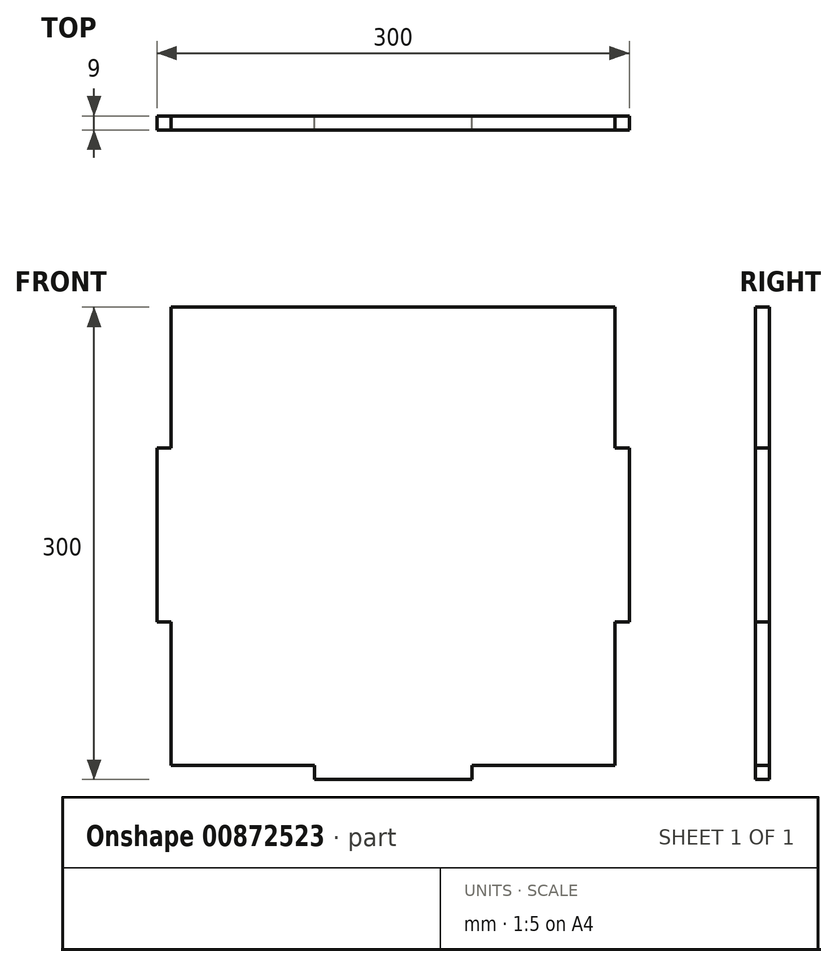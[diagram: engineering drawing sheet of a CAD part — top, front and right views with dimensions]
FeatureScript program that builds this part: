
annotation { "Feature Type Name" : "Feature", "Feature Type Description" : "" }
export const myFeature = defineFeature(function(context is Context, id is Id, definition is map)
    precondition{}
    {
        {
            var Q0;
            Q0=qCreatedBy(makeId("Front.planeOp"),FACE);
            var sketch = newSketch(context, id + "F0", { "sketchPlane" : qUnion([Q0])});
            skLineSegment(sketch, "E0.bottom", {"start": v(150, -150) * mm, "end": v(50, -150) * mm});
            skLineSegment(sketch, "E0.top", {"start": v(150, 150) * mm, "end": v(50, 150) * mm});
            skLineSegment(sketch, "E0.left", {"start": v(150, -150) * mm, "end": v(150, -50) * mm});
            skLineSegment(sketch, "E0.right", {"start": v(-150, -150) * mm, "end": v(-150, -50) * mm});
            skPoint(sketch, "E0.middle", {"position": v(0, 0) * mm});
            skLineSegment(sketch, "E1", {"start": v(-150, -50) * mm, "end": v(-141, -50) * mm});
            skLineSegment(sketch, "E2", {"start": v(-141, -50) * mm, "end": v(-141, 50) * mm});
            skLineSegment(sketch, "E3", {"start": v(-141, 50) * mm, "end": v(-150, 50) * mm});
            skLineSegment(sketch, "E4.trimOffspring", {"start": v(-150, 50) * mm, "end": v(-150, 150) * mm});
            skLineSegment(sketch, "E5", {"start": v(-50, 150) * mm, "end": v(-50, 141) * mm});
            skLineSegment(sketch, "E6", {"start": v(-50, 141) * mm, "end": v(50, 141) * mm});
            skLineSegment(sketch, "E7", {"start": v(50, 141) * mm, "end": v(50, 150) * mm});
            skLineSegment(sketch, "E8", {"start": v(150, 50) * mm, "end": v(141, 50) * mm});
            skLineSegment(sketch, "E9", {"start": v(141, 50) * mm, "end": v(141, -50) * mm});
            skLineSegment(sketch, "E10", {"start": v(141, -50) * mm, "end": v(150, -50) * mm});
            skLineSegment(sketch, "E11", {"start": v(-50, -150) * mm, "end": v(-50, -141) * mm});
            skLineSegment(sketch, "E12", {"start": v(-50, -141) * mm, "end": v(50, -141) * mm});
            skLineSegment(sketch, "E13", {"start": v(50, -141) * mm, "end": v(50, -150) * mm});
            skLineSegment(sketch, "E14.trimOffspring", {"start": v(150, 50) * mm, "end": v(150, 150) * mm});
            skLineSegment(sketch, "E15.trimOffspring", {"start": v(-50, -150) * mm, "end": v(-150, -150) * mm});
            skLineSegment(sketch, "E16", {"start": v(-50, 150) * mm, "end": v(-150, 150) * mm});
            skSolve(sketch);
        }
        {
            var Q0;
            Q0=makeQuery(id+"F0.imprint","IMPRINT",FACE,{"disambiguationData":[TD([[makeQuery(id+"F0.imprint","IMPRINT",EDGE,{"derivedFrom":sQuery(id+"F0.wireOp",EDGE,"E0.bottom")}),-1.0]])]});
            var sketch = newSketch(context, id + "F1", { "sketchPlane" : qUnion([Q0])});
            skLineSegment(sketch, "E17.top", {"start": v(141, 150) * mm, "end": v(-141, 150) * mm});
            skLineSegment(sketch, "E17.left", {"start": v(141, -141) * mm, "end": v(141, -50) * mm});
            skLineSegment(sketch, "E17.right", {"start": v(-141, -141) * mm, "end": v(-141, -50) * mm});
            skPoint(sketch, "E17.middle", {"position": v(0, 0) * mm});
            skLineSegment(sketch, "E18", {"start": v(141, 150) * mm, "end": v(141, 50) * mm});
            skLineSegment(sketch, "E19", {"start": v(141, 50) * mm, "end": v(150, 50) * mm});
            skLineSegment(sketch, "E20", {"start": v(150, 50) * mm, "end": v(150, -50) * mm});
            skLineSegment(sketch, "E21", {"start": v(150, -50) * mm, "end": v(141, -50) * mm});
            skLineSegment(sketch, "E22", {"start": v(-141, 150) * mm, "end": v(-141, 50) * mm});
            skLineSegment(sketch, "E23", {"start": v(-141, 50) * mm, "end": v(-150, 50) * mm});
            skLineSegment(sketch, "E24", {"start": v(-150, 50) * mm, "end": v(-150, -50) * mm});
            skLineSegment(sketch, "E25", {"start": v(-150, -50) * mm, "end": v(-141, -50) * mm});
            skLineSegment(sketch, "E26.trimOffspring", {"start": v(141, 50) * mm, "end": v(141, 150) * mm});
            skLineSegment(sketch, "E27.trimOffspring", {"start": v(-141, 50) * mm, "end": v(-141, 150) * mm});
            skLineSegment(sketch, "E28", {"start": v(-141, -50) * mm, "end": v(-141, -141) * mm});
            skLineSegment(sketch, "E29", {"start": v(-141, -141) * mm, "end": v(-50, -141) * mm});
            skLineSegment(sketch, "E30", {"start": v(-50, -141) * mm, "end": v(-50, -150) * mm});
            skLineSegment(sketch, "E31", {"start": v(50, -150) * mm, "end": v(50, -141) * mm});
            skLineSegment(sketch, "E32", {"start": v(50, -141) * mm, "end": v(141, -141) * mm});
            skPoint(sketch, "E33.orphan", {"position": v(-141, -150) * mm});
            skPoint(sketch, "E34.orphan", {"position": v(141, -150) * mm});
            skLineSegment(sketch, "E35", {"start": v(-50, -150) * mm, "end": v(50, -150) * mm});
            skSolve(sketch);
        }
        {
            var Q0;
            Q0=qCreatedBy(makeId("Right.planeOp"),FACE);
            var sketch = newSketch(context, id + "F2", { "sketchPlane" : qUnion([Q0])});
            skLineSegment(sketch, "E36.bottom", {"start": v(145.5, -150) * mm, "end": v(45.5, -150) * mm});
            skLineSegment(sketch, "E36.top", {"start": v(145.5, 150) * mm, "end": v(45.5, 150) * mm});
            skLineSegment(sketch, "E36.left", {"start": v(145.5, -135) * mm, "end": v(145.5, 150) * mm});
            skLineSegment(sketch, "E36.right", {"start": v(-145.5, -150) * mm, "end": v(-145.5, -50) * mm});
            skPoint(sketch, "E36.middle", {"position": v(0, 0) * mm});
            skLineSegment(sketch, "E37", {"start": v(45.5, 150) * mm, "end": v(45.5, 141) * mm});
            skLineSegment(sketch, "E38", {"start": v(45.5, 141) * mm, "end": v(-54.5, 141) * mm});
            skLineSegment(sketch, "E39", {"start": v(-54.5, 141) * mm, "end": v(-54.5, 150) * mm});
            skLineSegment(sketch, "E40.trimOffspring", {"start": v(-54.5, 150) * mm, "end": v(-145.5, 150) * mm});
            skLineSegment(sketch, "E41", {"start": v(130.5, -150) * mm, "end": v(45.5, -150) * mm});
            skLineSegment(sketch, "E42", {"start": v(45.5, -150) * mm, "end": v(45.5, -141) * mm});
            skLineSegment(sketch, "E43", {"start": v(45.5, -141) * mm, "end": v(-54.5, -141) * mm});
            skLineSegment(sketch, "E44", {"start": v(-54.5, -141) * mm, "end": v(-54.5, -150) * mm});
            skLineSegment(sketch, "E45", {"start": v(-145.5, 50) * mm, "end": v(-154.5, 50) * mm});
            skLineSegment(sketch, "E46", {"start": v(-154.5, 50) * mm, "end": v(-154.5, -50) * mm});
            skLineSegment(sketch, "E47", {"start": v(-154.5, -50) * mm, "end": v(-145.5, -50) * mm});
            skLineSegment(sketch, "E48.trimOffspring", {"start": v(-54.5, -150) * mm, "end": v(-145.5, -150) * mm});
            skLineSegment(sketch, "E49.trimOffspring", {"start": v(-145.5, 50) * mm, "end": v(-145.5, 150) * mm});
            skLineSegment(sketch, "E50", {"start": v(145.5, 150) * mm, "end": v(145.5, 125) * mm});
            skLineSegment(sketch, "E51", {"start": v(145.5, 125) * mm, "end": v(120.5, 125) * mm});
            skCircle(sketch, "E52", {"center": v(120.5, 125) * mm, "radius": 7.5 * mm});
            skPoint(sketch, "E53.visualSharp", {"position": v(145.5, -150) * mm});
            skArc(sketch, "E53.filletArc", {"start": v(130.5, -150) * mm, "mid": v(141.1, -145.6) * mm, "end": v(145.5, -135) * mm});
            skSolve(sketch);
        }
        {
            var Q0;
            Q0=qCreatedBy(makeId("Top.planeOp"),FACE);
            var sketch = newSketch(context, id + "F3", { "sketchPlane" : qUnion([Q0])});
            skLineSegment(sketch, "E54.bottom", {"start": v(140, -140) * mm, "end": v(60, -140) * mm});
            skLineSegment(sketch, "E54.top", {"start": v(140, 140) * mm, "end": v(-140, 140) * mm});
            skLineSegment(sketch, "E54.left", {"start": v(140, -140) * mm, "end": v(140, 131) * mm});
            skLineSegment(sketch, "E54.right", {"start": v(-140, -140) * mm, "end": v(-140, 131) * mm});
            skPoint(sketch, "E54.middle", {"position": v(0, 0) * mm});
            skLineSegment(sketch, "E55", {"start": v(140, 140) * mm, "end": v(149, 140) * mm});
            skLineSegment(sketch, "E56", {"start": v(149, 140) * mm, "end": v(149, 131) * mm});
            skLineSegment(sketch, "E57", {"start": v(149, 131) * mm, "end": v(140, 131) * mm});
            skLineSegment(sketch, "E58", {"start": v(-140, 140) * mm, "end": v(-149, 140) * mm});
            skLineSegment(sketch, "E59", {"start": v(-149, 140) * mm, "end": v(-149, 131) * mm});
            skLineSegment(sketch, "E60", {"start": v(-149, 131) * mm, "end": v(-140, 131) * mm});
            skLineSegment(sketch, "E61", {"start": v(-140, -140) * mm, "end": v(-60, -140) * mm});
            skLineSegment(sketch, "E62", {"start": v(-60, -140) * mm, "end": v(-60, -141) * mm});
            skLineSegment(sketch, "E63", {"start": v(-41, -160) * mm, "end": v(41, -160) * mm});
            skLineSegment(sketch, "E64", {"start": v(60, -141) * mm, "end": v(60, -140) * mm});
            skPoint(sketch, "E65.visualSharp", {"position": v(-60, -160) * mm});
            skArc(sketch, "E65.filletArc", {"start": v(-60, -141) * mm, "mid": v(-54.44, -154.44) * mm, "end": v(-41, -160) * mm});
            skPoint(sketch, "E66.visualSharp", {"position": v(60, -160) * mm});
            skArc(sketch, "E66.filletArc", {"start": v(41, -160) * mm, "mid": v(54.44, -154.44) * mm, "end": v(60, -141) * mm});
            skLineSegment(sketch, "E67.trimOffspring", {"start": v(-60, -140) * mm, "end": v(-140, -140) * mm});
            skSolve(sketch);
        }
        {
            var Q0;
            Q0=qCreatedBy(makeId("Front.planeOp"),FACE);
            var sketch = newSketch(context, id + "F4", { "sketchPlane" : qUnion([Q0])});
            skLineSegment(sketch, "E68.bottom", {"start": v(141, -130.5) * mm, "end": v(50, -130.5) * mm});
            skLineSegment(sketch, "E68.top", {"start": v(141, 130.5) * mm, "end": v(-141, 130.5) * mm});
            skLineSegment(sketch, "E68.left", {"start": v(141, -130.5) * mm, "end": v(141, -39.5) * mm});
            skLineSegment(sketch, "E68.right", {"start": v(-141, -130.5) * mm, "end": v(-141, -39.5) * mm});
            skPoint(sketch, "E68.middle", {"position": v(0, 0) * mm});
            skLineSegment(sketch, "E69", {"start": v(-141, -130.5) * mm, "end": v(-50, -130.5) * mm});
            skLineSegment(sketch, "E70", {"start": v(-50, -130.5) * mm, "end": v(-50, -139.5) * mm});
            skLineSegment(sketch, "E71", {"start": v(-50, -139.5) * mm, "end": v(50, -139.5) * mm});
            skLineSegment(sketch, "E72", {"start": v(50, -139.5) * mm, "end": v(50, -130.5) * mm});
            skLineSegment(sketch, "E73.trimOffspring", {"start": v(-50, -130.5) * mm, "end": v(-141, -130.5) * mm});
            skLineSegment(sketch, "E74", {"start": v(-141, -39.5) * mm, "end": v(-150, -39.5) * mm});
            skLineSegment(sketch, "E75", {"start": v(-150, -39.5) * mm, "end": v(-150, 60.5) * mm});
            skLineSegment(sketch, "E76", {"start": v(-150, 60.5) * mm, "end": v(-141, 60.5) * mm});
            skLineSegment(sketch, "E77.trimOffspring", {"start": v(-141, 60.5) * mm, "end": v(-141, 130.5) * mm});
            skLineSegment(sketch, "E78", {"start": v(141, -39.5) * mm, "end": v(150, -39.5) * mm});
            skLineSegment(sketch, "E79", {"start": v(150, -39.5) * mm, "end": v(150, 60.5) * mm});
            skLineSegment(sketch, "E80", {"start": v(150, 60.5) * mm, "end": v(141, 60.5) * mm});
            skLineSegment(sketch, "E81.trimOffspring", {"start": v(141, 60.5) * mm, "end": v(141, 130.5) * mm});
            skSolve(sketch);
        }
        {
            var Q0;
            Q0=qSketchRegion(id+"F4",true);
            extrude(context, id + "F5", {"entities" : qUnion([Q0]), "depth" : 9 * mm, "offsetDistance" : 25 * mm});
        }
        {
            var Q0;
            Q0=qSketchRegion(id+"F1",true);
            extrude(context, id + "F6", {"entities" : qUnion([Q0]), "operationType" : NewBodyOperationType.ADD, "depth" : 9 * mm, "offsetDistance" : 25 * mm});
        }
    });
